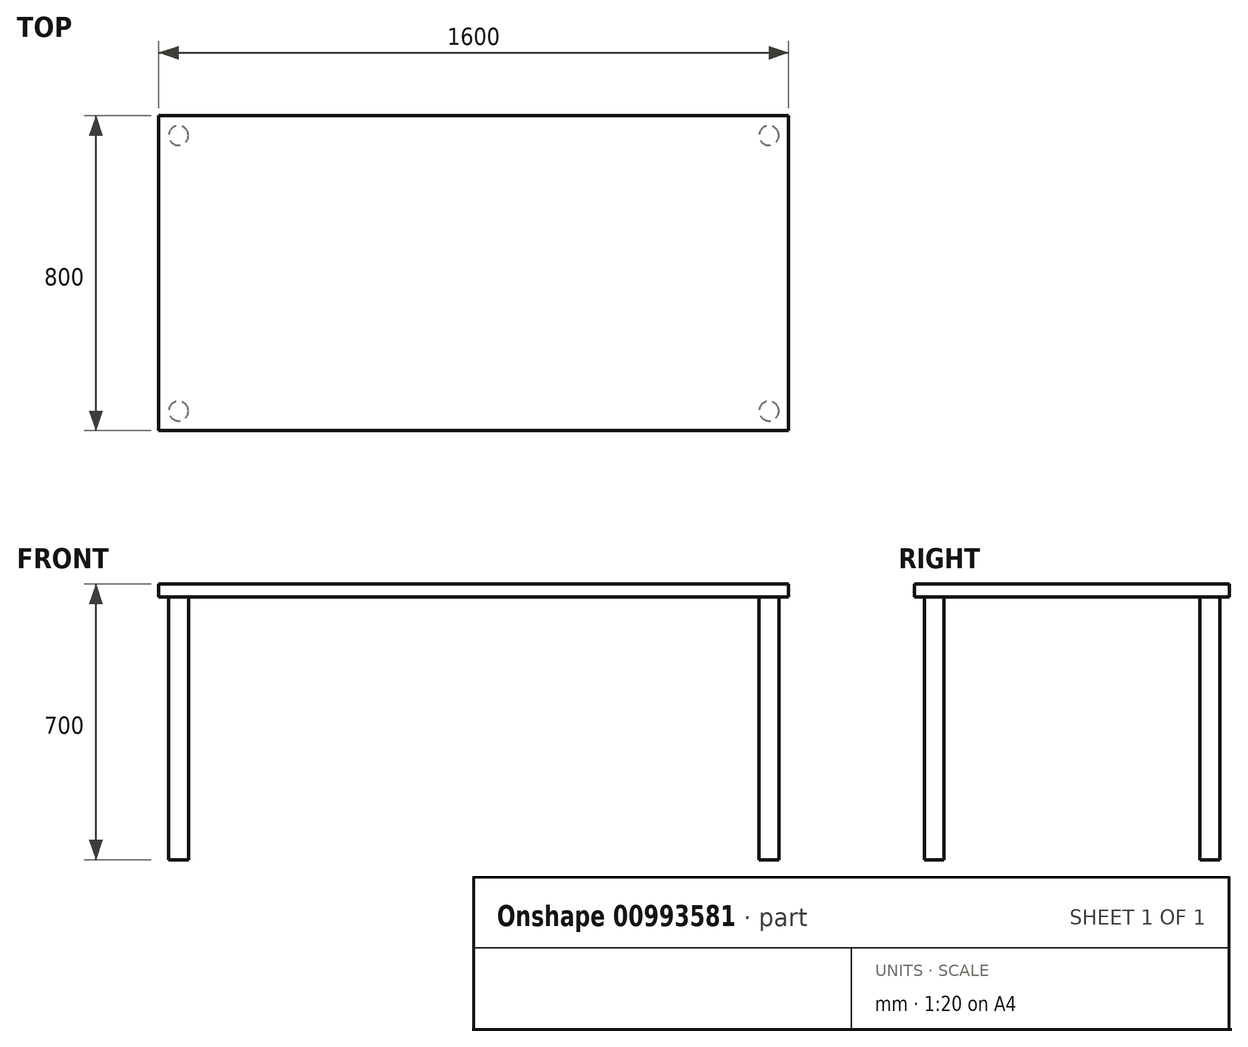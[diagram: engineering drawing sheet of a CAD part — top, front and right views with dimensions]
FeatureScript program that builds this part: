
annotation { "Feature Type Name" : "Feature", "Feature Type Description" : "" }
export const myFeature = defineFeature(function(context is Context, id is Id, definition is map)
    precondition{}
    {
        {
            assignVariable(context, id + "F0", {"name" : "tableHeight", "anyValue" : 700});
        }
        {
            var Q0;
            Q0=qCreatedBy(makeId("Top.planeOp"),FACE);
            var sketch = newSketch(context, id + "F1", { "sketchPlane" : qUnion([Q0])});
            skLineSegment(sketch, "E0.bottom", {"start": v(0, 0) * mm, "end": v(1600, 0) * mm});
            skLineSegment(sketch, "E0.top", {"start": v(0, 800) * mm, "end": v(1600, 800) * mm});
            skLineSegment(sketch, "E0.left", {"start": v(0, 0) * mm, "end": v(0, 800) * mm});
            skLineSegment(sketch, "E0.right", {"start": v(1600, 0) * mm, "end": v(1600, 800) * mm});
            skSolve(sketch);
        }
        {
            var Q0;
            Q0 = qSketchRegion(id + "F1", true);
            extrude(context, id + "F2", {"entities" : qUnion([Q0]), "oppositeDirection" : true, "depth" : 33 * mm, "offsetDistance" : 25 * mm});
        }
        {
            var Q0;
            Q0=qCreatedBy(makeId("Top.planeOp"),FACE);
            var sketch = newSketch(context, id + "F3", { "sketchPlane" : qUnion([Q0])});
            skLineSegment(sketch, "E1.0.0", {"start": v(1600, 800) * mm, "end": v(0, 800) * mm, "construction": true});
            skLineSegment(sketch, "E1.0.1", {"start": v(1600, 0) * mm, "end": v(1600, 800) * mm, "construction": true});
            skLineSegment(sketch, "E1.0.2", {"start": v(0, 0) * mm, "end": v(1600, 0) * mm, "construction": true});
            skLineSegment(sketch, "E1.0.3", {"start": v(0, 800) * mm, "end": v(0, 0) * mm, "construction": true});
            skCircle(sketch, "E2", {"center": v(1550, 50) * mm, "radius": 25 * mm});
            skCircle(sketch, "E3", {"center": v(1550, 750) * mm, "radius": 25 * mm});
            skCircle(sketch, "E4", {"center": v(50, 750) * mm, "radius": 25 * mm});
            skCircle(sketch, "E5", {"center": v(50, 50) * mm, "radius": 25 * mm});
            skLineSegment(sketch, "E6.bottom", {"start": v(1550, 50) * mm, "end": v(50, 50) * mm, "construction": true});
            skLineSegment(sketch, "E6.top", {"start": v(50, 750) * mm, "end": v(1550, 750) * mm, "construction": true});
            skLineSegment(sketch, "E6.left", {"start": v(50, 50) * mm, "end": v(50, 750) * mm, "construction": true});
            skLineSegment(sketch, "E6.right", {"start": v(1550, 750) * mm, "end": v(1550, 50) * mm, "construction": true});
            skPoint(sketch, "E6.middle", {"position": v(800, 400) * mm});
            skLineSegment(sketch, "E7", {"start": v(800, 0) * mm, "end": v(800, 800) * mm, "construction": true});
            skLineSegment(sketch, "E8", {"start": v(1600, 400) * mm, "end": v(0, 400) * mm, "construction": true});
            skSolve(sketch);
        }
        {
            var Q0;
            Q0 = qSketchRegion(id + "F3", true);
            extrude(context, id + "F4", {"entities" : qUnion([Q0]), "operationType" : NewBodyOperationType.ADD, "oppositeDirection" : true, "depth" : (getVariable(context, 'tableHeight')) * mm, "offsetDistance" : 25 * mm});
        }
    });
